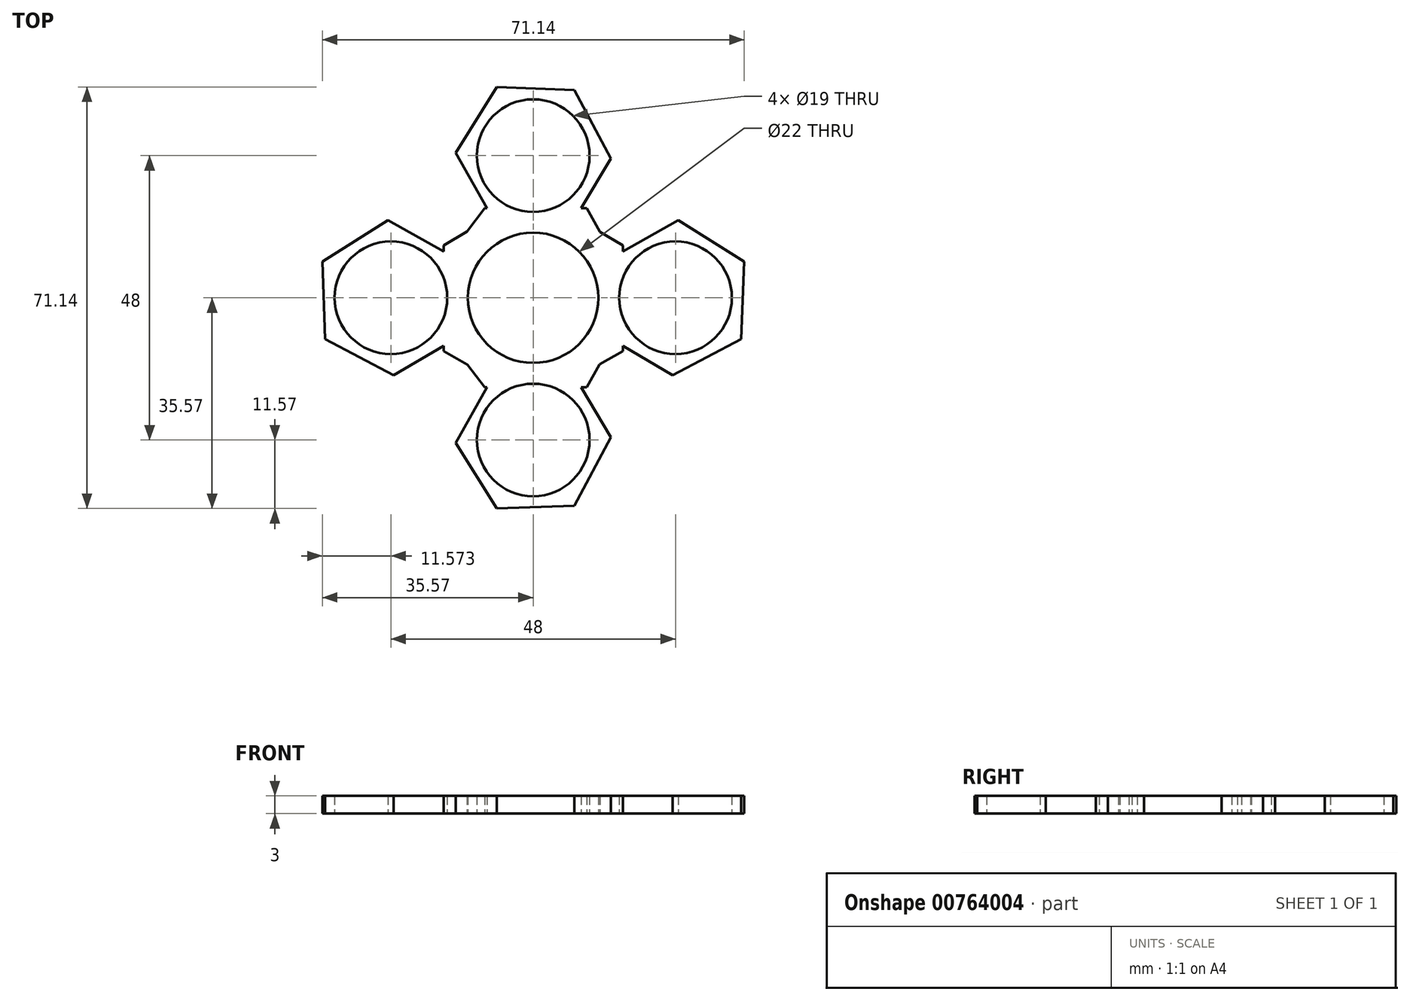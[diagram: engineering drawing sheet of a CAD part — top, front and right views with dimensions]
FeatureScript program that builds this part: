
annotation { "Feature Type Name" : "Feature", "Feature Type Description" : "" }
export const myFeature = defineFeature(function(context is Context, id is Id, definition is map)
    precondition{}
    {
        {
            var Q0;
            Q0=qCreatedBy(makeId("Top.planeOp"),FACE);
            var sketch = newSketch(context, id + "F0", { "sketchPlane" : qUnion([Q0])});
            skArc(sketch, "E0", {"start": v(11, 0) * mm, "mid": v(0, 11) * mm, "end": v(-11, 0) * mm});
            skLineSegment(sketch, "E1.0", {"start": v(9.02, 15.1) * mm, "end": v(11.24, 11.1) * mm});
            skLineSegment(sketch, "E1.5", {"start": v(-8.19, 15.1) * mm, "end": v(-7.81, 15.1) * mm});
            skPoint(sketch, "E1.0.midPoint", {"position": v(13.3, 7.4) * mm});
            skCircle(sketch, "E2", {"center": v(0, 24) * mm, "radius": 9.5 * mm});
            skLineSegment(sketch, "E3.0", {"start": v(13.08, 23.52) * mm, "end": v(8.11, 15.1) * mm});
            skLineSegment(sketch, "E3.3", {"start": v(-13.08, 24.48) * mm, "end": v(-6.12, 35.57) * mm});
            skLineSegment(sketch, "E3.4", {"start": v(-6.12, 35.57) * mm, "end": v(6.96, 35.09) * mm});
            skLineSegment(sketch, "E3.5", {"start": v(6.96, 35.09) * mm, "end": v(13.08, 23.52) * mm});
            skPoint(sketch, "E3.0.midPoint", {"position": v(9.76, 17.89) * mm});
            skLineSegment(sketch, "E4.trimOffspring", {"start": v(8.11, 15.1) * mm, "end": v(9.02, 15.1) * mm});
            skLineSegment(sketch, "E5.trimOffspring", {"start": v(-13.76, 7.72) * mm, "end": v(-13.76, 7.72) * mm});
            skLineSegment(sketch, "E6.trimOffspring", {"start": v(-7.81, 15.1) * mm, "end": v(-13.08, 24.48) * mm});
            skPoint(sketch, "E7.orphan", {"position": v(6.44, 12.26) * mm});
            skPoint(sketch, "E8", {"position": v(-7.81, 15.1) * mm});
            skPoint(sketch, "E9", {"position": v(-11, 0) * mm});
            skPoint(sketch, "E10", {"position": v(11, 0) * mm});
            skLineSegment(sketch, "E11.MirrorCS", {"start": v(-8.19, -15.1) * mm, "end": v(-7.81, -15.1) * mm});
            skLineSegment(sketch, "E12.MirrorCS", {"start": v(8.11, -15.1) * mm, "end": v(9.02, -15.1) * mm});
            skLineSegment(sketch, "E13.MirrorCS", {"start": v(0, -12.66) * mm, "end": v(0, -12.67) * mm});
            skLineSegment(sketch, "E14.MirrorCS", {"start": v(13.08, -23.52) * mm, "end": v(8.11, -15.1) * mm});
            skLineSegment(sketch, "E15.MirrorCS", {"start": v(-13.76, -7.72) * mm, "end": v(-13.76, -7.72) * mm});
            skCircle(sketch, "E16.MirrorC", {"center": v(0, -24) * mm, "radius": 9.5 * mm});
            skLineSegment(sketch, "E17.MirrorCS", {"start": v(-13.08, -24.48) * mm, "end": v(-6.12, -35.57) * mm});
            skArc(sketch, "E18.MirrorCS", {"start": v(11, 0) * mm, "mid": v(0, -11) * mm, "end": v(-11, 0) * mm});
            skPoint(sketch, "E19.MirrorP", {"position": v(13.3, -7.4) * mm});
            skPoint(sketch, "E20.MirrorP", {"position": v(6.44, -12.26) * mm});
            skPoint(sketch, "E21.MirrorP", {"position": v(-7.81, -15.1) * mm});
            skPoint(sketch, "E22.MirrorP", {"position": v(9.76, -17.89) * mm});
            skLineSegment(sketch, "E23.MirrorCS", {"start": v(-6.12, -35.57) * mm, "end": v(6.96, -35.09) * mm});
            skLineSegment(sketch, "E24.MirrorCS", {"start": v(-7.81, -15.1) * mm, "end": v(-13.08, -24.48) * mm});
            skLineSegment(sketch, "E25.MirrorCS", {"start": v(9.02, -15.1) * mm, "end": v(11.18, -11.23) * mm});
            skLineSegment(sketch, "E26.MirrorCS", {"start": v(6.96, -35.09) * mm, "end": v(13.08, -23.52) * mm});
            skLineSegment(sketch, "E27.0", {"start": v(15.1, -9.01) * mm, "end": v(11.18, -11.23) * mm});
            skLineSegment(sketch, "E27.5", {"start": v(15.1, 8.81) * mm, "end": v(15.1, 7.82) * mm});
            skPoint(sketch, "E27.0.midPoint", {"position": v(7.45, -13.32) * mm});
            skCircle(sketch, "E28", {"center": v(24, 0) * mm, "radius": 9.5 * mm});
            skLineSegment(sketch, "E29.0", {"start": v(23.52, -13.07) * mm, "end": v(15.1, -8.1) * mm});
            skLineSegment(sketch, "E29.3", {"start": v(24.49, 13.09) * mm, "end": v(35.57, 6.13) * mm});
            skLineSegment(sketch, "E29.4", {"start": v(35.57, 6.13) * mm, "end": v(35.09, -6.95) * mm});
            skLineSegment(sketch, "E29.5", {"start": v(35.09, -6.95) * mm, "end": v(23.52, -13.07) * mm});
            skPoint(sketch, "E29.0.midPoint", {"position": v(17.9, -9.75) * mm});
            skLineSegment(sketch, "E30.trimOffspring", {"start": v(15.1, -8.1) * mm, "end": v(15.1, -9.01) * mm});
            skLineSegment(sketch, "E31.trimOffspring", {"start": v(15.1, 7.82) * mm, "end": v(24.49, 13.09) * mm});
            skPoint(sketch, "E32.orphan", {"position": v(12.26, -6.43) * mm});
            skPoint(sketch, "E33", {"position": v(15.1, 7.82) * mm});
            skPoint(sketch, "E34", {"position": v(0, 11) * mm});
            skPoint(sketch, "E35", {"position": v(0, -11) * mm});
            skLineSegment(sketch, "E36.MirrorCS", {"start": v(-7.63, -13.22) * mm, "end": v(-7.63, -13.22) * mm});
            skArc(sketch, "E37.MirrorCS", {"start": v(-7.44, -13.32) * mm, "mid": v(-7.54, -13.27) * mm, "end": v(-7.63, -13.22) * mm, "construction": true});
            skLineSegment(sketch, "E38.MirrorCS", {"start": v(-15.1, 8.81) * mm, "end": v(-15.1, 7.82) * mm});
            skLineSegment(sketch, "E39.MirrorCS", {"start": v(-15.1, -8.1) * mm, "end": v(-15.1, -9.01) * mm});
            skLineSegment(sketch, "E40.MirrorCS", {"start": v(-23.51, -13.07) * mm, "end": v(-15.1, -8.1) * mm});
            skCircle(sketch, "E41.MirrorC", {"center": v(-24, 0) * mm, "radius": 9.5 * mm});
            skLineSegment(sketch, "E42.MirrorCS", {"start": v(-24.48, 13.09) * mm, "end": v(-35.57, 6.13) * mm});
            skPoint(sketch, "E43.MirrorP", {"position": v(-7.44, -13.32) * mm});
            skPoint(sketch, "E44.MirrorP", {"position": v(-12.26, -6.43) * mm});
            skPoint(sketch, "E45.MirrorP", {"position": v(-15.1, 7.82) * mm});
            skPoint(sketch, "E46.MirrorP", {"position": v(-17.88, -9.75) * mm});
            skLineSegment(sketch, "E47.MirrorCS", {"start": v(-35.57, 6.13) * mm, "end": v(-35.08, -6.95) * mm});
            skLineSegment(sketch, "E48.MirrorCS", {"start": v(-15.1, 7.82) * mm, "end": v(-24.48, 13.09) * mm});
            skLineSegment(sketch, "E49.MirrorCS", {"start": v(-15.1, -9.01) * mm, "end": v(-11.07, -11.28) * mm});
            skLineSegment(sketch, "E50.MirrorCS", {"start": v(-35.08, -6.95) * mm, "end": v(-23.51, -13.07) * mm});
            skLineSegment(sketch, "E51.trimOffspring", {"start": v(-11.14, 11.16) * mm, "end": v(-15.1, 8.81) * mm});
            skLineSegment(sketch, "E52.trimOffspring", {"start": v(-11.14, 11.16) * mm, "end": v(-8.19, 15.1) * mm});
            skPoint(sketch, "E1.4.start.orphan", {"position": v(-18.78, 1.07) * mm});
            skPoint(sketch, "E53.orphan", {"position": v(-18.78, -1.07) * mm});
            skLineSegment(sketch, "E54.trimOffspring", {"start": v(-11.07, -11.28) * mm, "end": v(-8.19, -15.1) * mm});
            skLineSegment(sketch, "E55.trimOffspring", {"start": v(-7.63, -13.22) * mm, "end": v(-7.44, -13.32) * mm});
            skLineSegment(sketch, "E56.trimOffspring", {"start": v(11.24, 11.1) * mm, "end": v(15.1, 8.81) * mm});
            skPoint(sketch, "E57.trimOffspring.start.orphan", {"position": v(13.2, 7.59) * mm});
            skPoint(sketch, "E58.trimOffspring.start.orphan", {"position": v(13.18, 7.61) * mm});
            skPoint(sketch, "E59.trimOffspring.end.orphan", {"position": v(0, 12.67) * mm});
            skPoint(sketch, "E59.trimOffspring.start.orphan", {"position": v(0, 12.66) * mm});
            skPoint(sketch, "E60.trimOffspring.end.orphan", {"position": v(0, 15.28) * mm});
            skPoint(sketch, "E60.trimOffspring.start.orphan", {"position": v(0, 15.28) * mm});
            skPoint(sketch, "E61.trimOffspring.end.orphan", {"position": v(17.59, 0.31) * mm});
            skPoint(sketch, "E62.trimOffspring.end.orphan", {"position": v(17.59, -0.31) * mm});
            skPoint(sketch, "E63.MirrorCS.start.orphan", {"position": v(13.2, -7.59) * mm});
            skPoint(sketch, "E64.trimOffspring.start.orphan", {"position": v(13.18, -7.61) * mm});
            skPoint(sketch, "E65.trimOffspring.end.orphan", {"position": v(-0.21, -17.64) * mm});
            skPoint(sketch, "E66.MirrorCS.end.orphan", {"position": v(0, -15.28) * mm});
            skPoint(sketch, "E66.MirrorCS.start.orphan", {"position": v(0, -15.28) * mm});
            skSolve(sketch);
        }
        {
            var Q0;
            Q0 = qSketchRegion(id + "F0", true);
            extrude(context, id + "F1", {"entities" : qUnion([Q0]), "depth" : 3 * mm, "offsetDistance" : 25 * mm});
        }
    });
